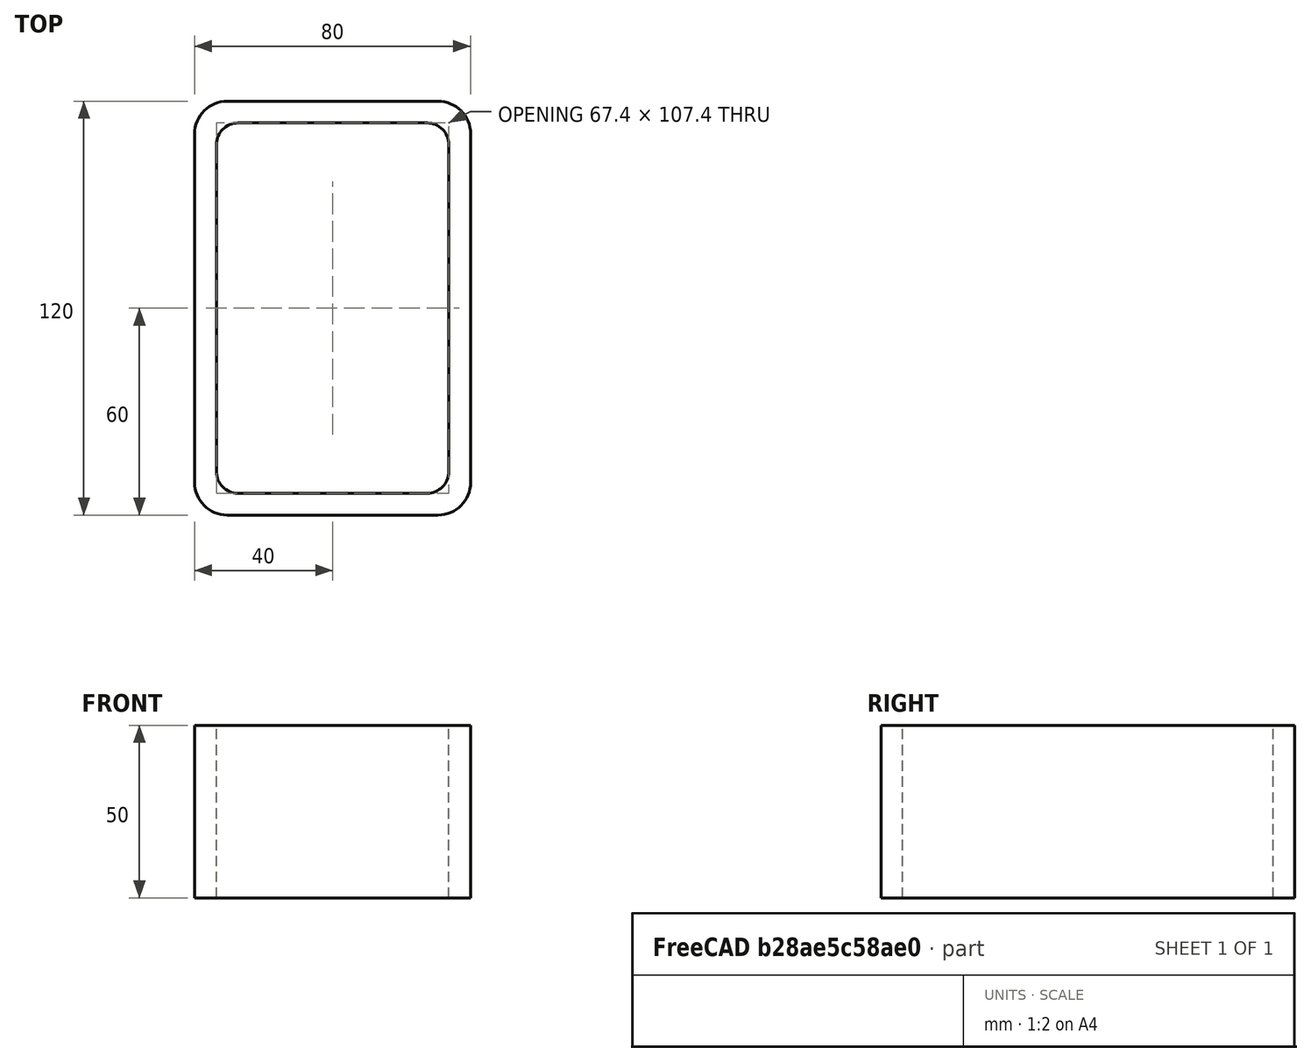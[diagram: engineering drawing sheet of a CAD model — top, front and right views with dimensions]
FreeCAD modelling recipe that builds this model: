
FCSTD DOCUMENT  (FreeCAD 0.15R4671 (Git))
Label: Rectangular hollow section 120x80x6.3 EN10219 S235JRH
License: All rights reserved
LicenseURL: http://en.wikipedia.org/wiki/All_rights_reserved
objects: Sketcher::SketchObject×1, Part::Extrusion×1
note: 2 computed .brp shape members not serialized (recipe doc carries the construction recipe); baked Part::Feature solids carry a one-line shape summary decoded from their .brp

FEATURE [Sketcher::SketchObject] Sketch
  sketch-geometry (16):
    g0: LineSegment StartX=-27.4 StartY=53.7 StartZ=0 EndX=27.4 EndY=53.7 EndZ=0
    g1: LineSegment StartX=33.7 StartY=47.4 StartZ=0 EndX=33.7 EndY=-47.4 EndZ=0
    g2: LineSegment StartX=27.4 StartY=-53.7 StartZ=0 EndX=-27.4 EndY=-53.7 EndZ=0
    g3: LineSegment StartX=-33.7 StartY=-47.4 StartZ=0 EndX=-33.7 EndY=47.4 EndZ=0
    g4: LineSegment StartX=-30.55 StartY=60 StartZ=0 EndX=30.55 EndY=60 EndZ=0
    g5: LineSegment StartX=40 StartY=50.55 StartZ=0 EndX=40 EndY=-50.55 EndZ=0
    g6: LineSegment StartX=30.55 StartY=-60 StartZ=0 EndX=-30.55 EndY=-60 EndZ=0
    g7: LineSegment StartX=-40 StartY=-50.55 StartZ=0 EndX=-40 EndY=50.55 EndZ=0
    g8: ArcOfCircle CenterX=-27.4 CenterY=47.4 CenterZ=0 NormalX=0 NormalY=0 NormalZ=1 Radius=6.3 StartAngle=1.5708 EndAngle=3.14159
    g9: ArcOfCircle CenterX=27.4 CenterY=47.4 CenterZ=0 NormalX=0 NormalY=0 NormalZ=1 Radius=6.3 StartAngle=0 EndAngle=1.5708
    g10: ArcOfCircle CenterX=27.4 CenterY=-47.4 CenterZ=0 NormalX=0 NormalY=0 NormalZ=1 Radius=6.3 StartAngle=4.71239 EndAngle=6.28319
    g11: ArcOfCircle CenterX=-27.4 CenterY=-47.4 CenterZ=0 NormalX=0 NormalY=0 NormalZ=1 Radius=6.3 StartAngle=3.14159 EndAngle=4.71239
    g12: ArcOfCircle CenterX=30.55 CenterY=50.55 CenterZ=0 NormalX=0 NormalY=0 NormalZ=1 Radius=9.45 StartAngle=0 EndAngle=1.5708
    g13: ArcOfCircle CenterX=30.55 CenterY=-50.55 CenterZ=0 NormalX=0 NormalY=0 NormalZ=1 Radius=9.45 StartAngle=4.71239 EndAngle=6.28319
    g14: ArcOfCircle CenterX=-30.55 CenterY=-50.55 CenterZ=0 NormalX=0 NormalY=0 NormalZ=1 Radius=9.45 StartAngle=3.14159 EndAngle=4.71239
    g15: ArcOfCircle CenterX=-30.55 CenterY=50.55 CenterZ=0 NormalX=0 NormalY=0 NormalZ=1 Radius=9.45 StartAngle=1.5708 EndAngle=3.14159
  constraints (36):
    c: Horizontal(g2)
    c: Vertical(g3)
    c: Horizontal(g6)
    c: Vertical(g7)
    c: Tangent(g3,g8) = 1.5708
    c: Tangent(g0,g8) = 1.5708
    c: Tangent(g0,g9) = 1.5708
    c: Tangent(g1,g9) = 1.5708
    c: Tangent(g1,g10) = 1.5708
    c: Tangent(g2,g10) = 1.5708
    c: Tangent(g2,g11) = 1.5708
    c: Tangent(g3,g11) = 1.5708
    c: Tangent(g4,g12) = 1.5708
    c: Tangent(g5,g12) = 1.5708
    c: Tangent(g5,g13) = 1.5708
    c: Tangent(g6,g13) = 1.5708
    c: Tangent(g6,g14) = 1.5708
    c: Tangent(g7,g14) = 1.5708
    c: Tangent(g7,g15) = 1.5708
    c: Tangent(g4,g15) = 1.5708
    c: Equal(g9,g8)
    c: Equal(g9,g11)
    c: Equal(g9,g10)
    c: Equal(g12,g15)
    c: Equal(g12,g14)
    c: Equal(g12,g13)
    c: Symmetric(g4,g6,g-1)
    c: Symmetric(g7,g5,g-2)
    c: DistanceY(g4,g6) = -120
    c: DistanceX(g7,g5) = 80
    c: Symmetric(g3,g1,g-2)
    c: Symmetric(g0,g2,g-1)
    c: DistanceY(g0,g4) = 6.3
    c: DistanceX(g5,g1) = -6.3
    c: Radius(g9) = 6.3
    c: Radius(g12) = 9.45
FEATURE [Part::Extrusion] Extrude  label="Rectangular hollow section 120x80x6.3 EN10219 S235JRH"
  Base = -> Sketch
  Dir = (0,0,50)
  Solid = true
